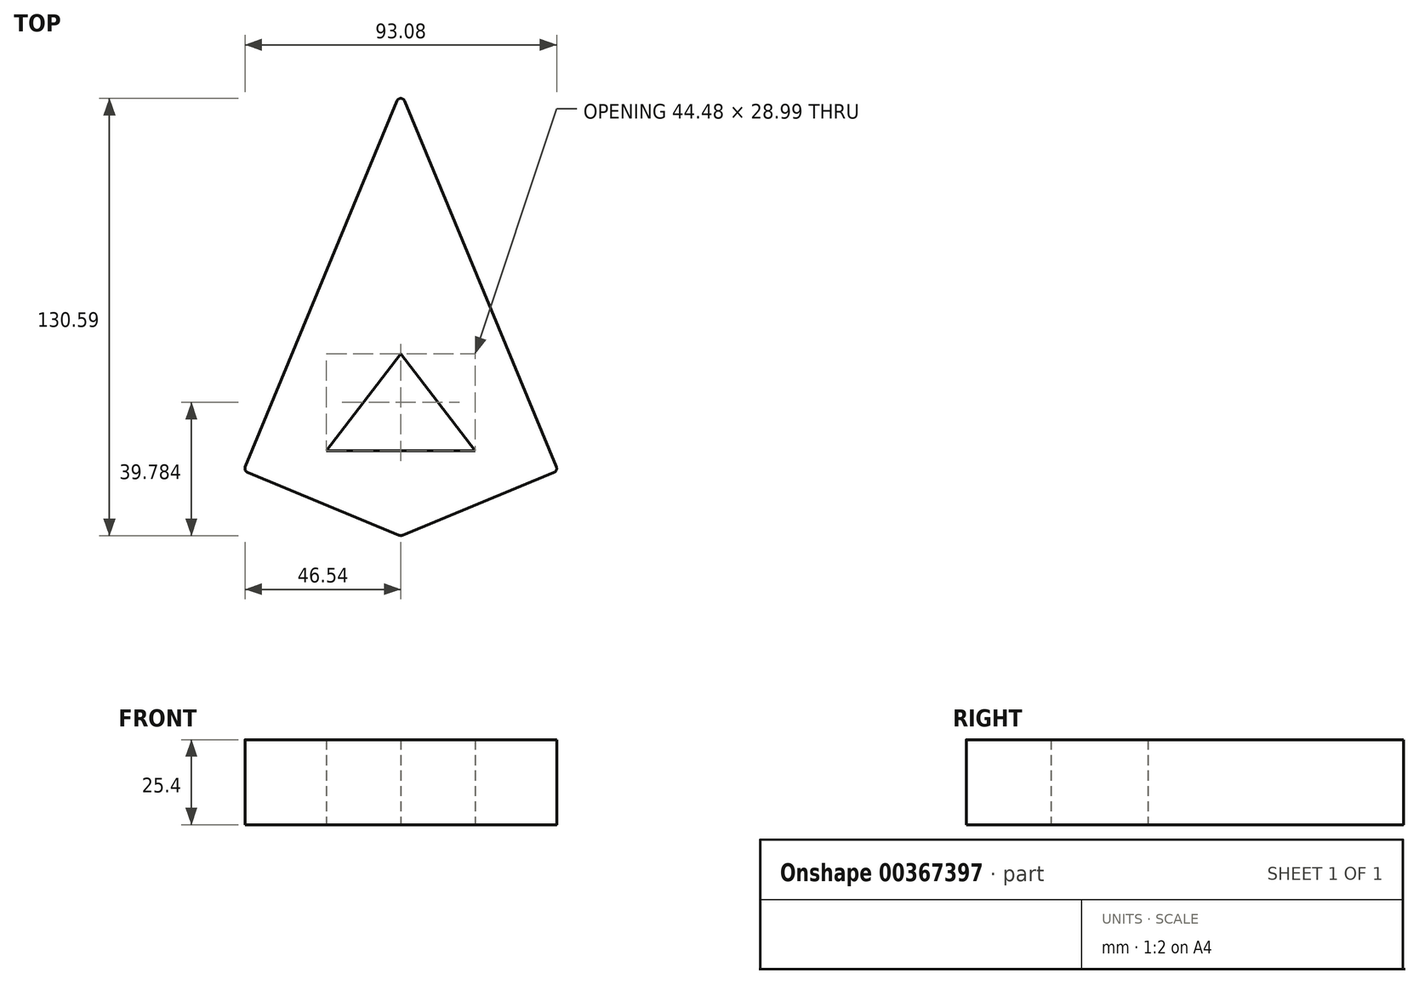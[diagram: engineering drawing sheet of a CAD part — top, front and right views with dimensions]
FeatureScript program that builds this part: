
annotation { "Feature Type Name" : "Feature", "Feature Type Description" : "" }
export const myFeature = defineFeature(function(context is Context, id is Id, definition is map)
    precondition{}
    {
        {
            var Q0;
            Q0=qCreatedBy(makeId("Top.planeOp"),FACE);
            var sketch = newSketch(context, id + "F0", { "sketchPlane" : qUnion([Q0])});
            skLineSegment(sketch, "E0", {"start": v(0, 78.09) * mm, "end": v(-46.93, -35.22) * mm});
            skLineSegment(sketch, "E1", {"start": v(-46.93, -35.22) * mm, "end": v(0, -54.66) * mm});
            skLineSegment(sketch, "E2", {"start": v(0, -54.66) * mm, "end": v(46.93, -35.22) * mm});
            skLineSegment(sketch, "E3", {"start": v(46.93, -35.22) * mm, "end": v(0, 78.09) * mm});
            skLineSegment(sketch, "E4", {"start": v(0, 0) * mm, "end": v(0, 78.09) * mm, "construction": true});
            skLineSegment(sketch, "E5", {"start": v(-22.24, -29.26) * mm, "end": v(22.24, -29.26) * mm});
            skLineSegment(sketch, "E6", {"start": v(22.24, -29.26) * mm, "end": v(0, -0.27) * mm});
            skLineSegment(sketch, "E7", {"start": v(0, -0.27) * mm, "end": v(-22.24, -29.26) * mm});
            skSolve(sketch);
        }
        {
            var Q0;
            Q0 = qSketchRegion(id + "F0", true);
            extrude(context, id + "F1", {"entities" : qUnion([Q0]), "depth" : 25.4 * mm});
        }
        {
            var Q0;
            Q0=makeQuery(id+"F1.opExtrude","SWEPT_EDGE",EDGE,{"disambiguationData":[OSD([sQuery(id+"F0.wireOp",EDGE,"E1"),sQuery(id+"F0.wireOp",EDGE,"E2")])]});
            var Q1;
            Q1=makeQuery(id+"F1.opExtrude","SWEPT_EDGE",EDGE,{"disambiguationData":[OSD([sQuery(id+"F0.wireOp",EDGE,"E2"),sQuery(id+"F0.wireOp",EDGE,"E3")])]});
            var Q2;
            Q2=makeQuery(id+"F1.opExtrude","SWEPT_EDGE",EDGE,{"disambiguationData":[OSD([sQuery(id+"F0.wireOp",EDGE,"E0"),sQuery(id+"F0.wireOp",EDGE,"E3")])]});
            var Q3;
            Q3=makeQuery(id+"F1.opExtrude","SWEPT_EDGE",EDGE,{"disambiguationData":[OSD([sQuery(id+"F0.wireOp",EDGE,"E0"),sQuery(id+"F0.wireOp",EDGE,"E1")])]});
            fillet(context, id + "F2", {"entities" : qUnion([Q0, Q1, Q2, Q3]), "radius" : 1.27 * mm, "tangentPropagation" : true, "allowEdgeOverflow" : false});
        }
    });
